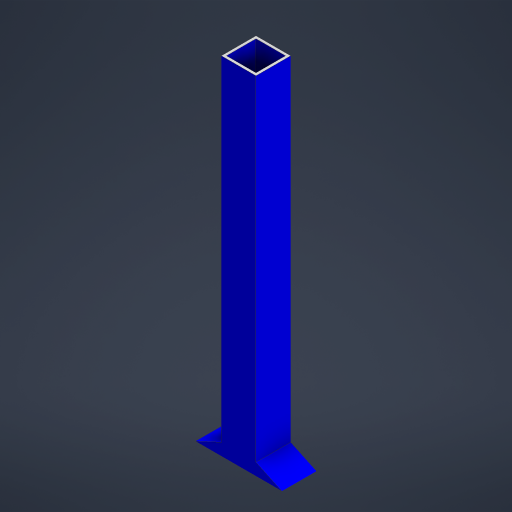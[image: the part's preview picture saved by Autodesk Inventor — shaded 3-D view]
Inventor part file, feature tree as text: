
AUTODESK INVENTOR PART (.ipt)
format: ipt  version: 2024 (Build 280153000, 153)  size: 201,216 bytes
history: native  units: mm
features: other x5, extrude x1, sketch x1, projected_geometry x1
ambient origin geometry x8: Origin, YZ Plane, XZ Plane, XY Plane, X Axis, Y Axis, Z Axis, Center Point
bodies: Body1 (feature_tree)
feature tree (8):
  other  "shock_absorber_holder_down_150.ipt"
  extrude  "Выдавливание1"  Depth=10.0mm
  other  "Твердое тело1::shock_absorber_holder_down_150.ipt"
  other  "Элемент создания тегов1"
  other  "РабПлоскость1"
  sketch  "Эскиз1"
  projected_geometry  "Спроецированная петля1"
  other  "Твердое тело1"
